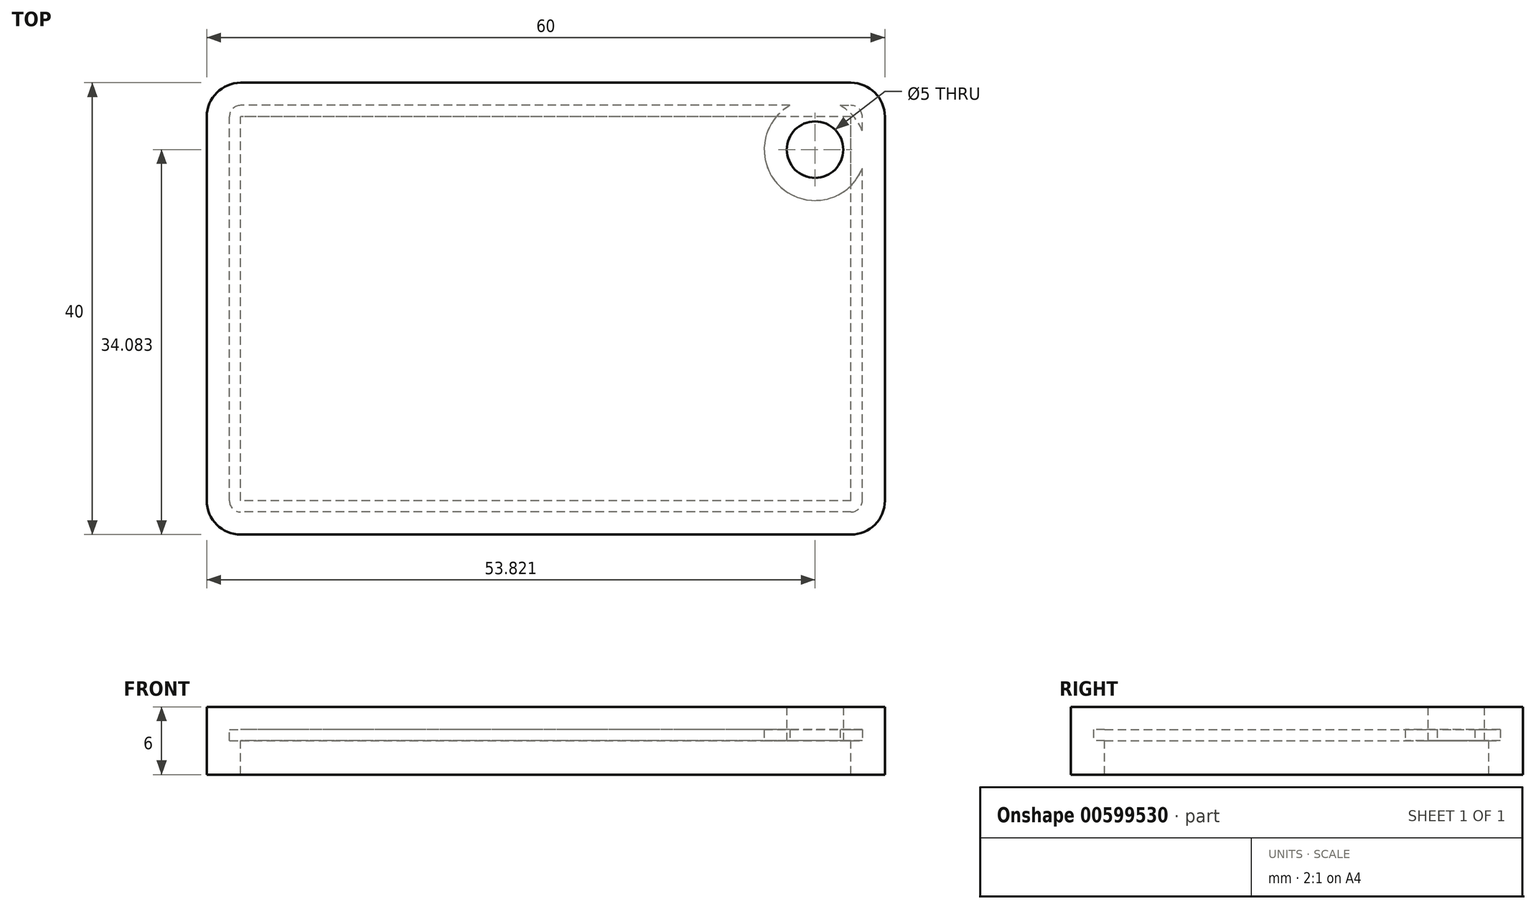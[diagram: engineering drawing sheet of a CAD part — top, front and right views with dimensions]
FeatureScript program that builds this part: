
annotation { "Feature Type Name" : "Feature", "Feature Type Description" : "" }
export const myFeature = defineFeature(function(context is Context, id is Id, definition is map)
    precondition{}
    {
        {
            var Q0;
            Q0=qCreatedBy(makeId("Top.planeOp"),FACE);
            var sketch = newSketch(context, id + "F0", { "sketchPlane" : qUnion([Q0])});
            skLineSegment(sketch, "E0.bottom", {"start": v(30, -20) * mm, "end": v(-30, -20) * mm});
            skLineSegment(sketch, "E0.top", {"start": v(30, 20) * mm, "end": v(-30, 20) * mm});
            skLineSegment(sketch, "E0.left", {"start": v(30, -20) * mm, "end": v(30, 20) * mm});
            skLineSegment(sketch, "E0.right", {"start": v(-30, -20) * mm, "end": v(-30, 20) * mm});
            skPoint(sketch, "E0.middle", {"position": v(0, 0) * mm});
            skSolve(sketch);
        }
        {
            var Q0;
            Q0=makeQuery(id+"F0.imprint","IMPRINT",FACE,{"disambiguationData":[TD([[makeQuery(id+"F0.imprint","IMPRINT",EDGE,{"derivedFrom":sQuery(id+"F0.wireOp",EDGE,"E0.bottom")}),-1.0]])]});
            extrude(context, id + "F1", {"entities" : qUnion([Q0]), "depth" : 6 * mm, "offsetDistance" : 25 * mm});
        }
        {
            var Q0;
            Q0=makeQuery(id+"F1.opExtrude","SWEPT_EDGE",EDGE,{"disambiguationData":[OSD([sQuery(id+"F0.wireOp",EDGE,"E0.bottom"),sQuery(id+"F0.wireOp",EDGE,"E0.right")])]});
            var Q1;
            Q1=makeQuery(id+"F1.opExtrude","SWEPT_EDGE",EDGE,{"disambiguationData":[OSD([sQuery(id+"F0.wireOp",EDGE,"E0.bottom"),sQuery(id+"F0.wireOp",EDGE,"E0.left")])]});
            var Q2;
            Q2=makeQuery(id+"F1.opExtrude","SWEPT_EDGE",EDGE,{"disambiguationData":[OSD([sQuery(id+"F0.wireOp",EDGE,"E0.top"),sQuery(id+"F0.wireOp",EDGE,"E0.right")])]});
            var Q3;
            Q3=makeQuery(id+"F1.opExtrude","SWEPT_EDGE",EDGE,{"disambiguationData":[OSD([sQuery(id+"F0.wireOp",EDGE,"E0.top"),sQuery(id+"F0.wireOp",EDGE,"E0.left")])]});
            fillet(context, id + "F2", {"entities" : qUnion([Q0, Q1, Q2, Q3]), "radius" : 3 * mm, "tangentPropagation" : true, "allowEdgeOverflow" : false});
        }
        {
            var Q0;
            Q0=makeQuery(id+"F1.opExtrude","CAP_FACE",FACE,{"disambiguationData":[OSD([sQuery(id+"F0.wireOp",EDGE,"E0.bottom"),sQuery(id+"F0.wireOp",EDGE,"E0.top"),sQuery(id+"F0.wireOp",EDGE,"E0.left"),sQuery(id+"F0.wireOp",EDGE,"E0.right")])],"isStart":true});
            shell(context, id + "F3", {"entities" : qUnion([Q0]), "thickness" : 3 * mm});
        }
        {
            var Q0;
            Q0=qCreatedBy(makeId("Top.planeOp"),FACE);
            var sketch = newSketch(context, id + "F4", { "sketchPlane" : qUnion([Q0])});
            skCircle(sketch, "E1", {"center": v(23.82, 14.08) * mm, "radius": 2.8 * mm});
            skPoint(sketch, "E1.first.point", {"position": v(25.9, 15.98) * mm});
            skPoint(sketch, "E1.second.point", {"position": v(22.28, 11.73) * mm});
            skPoint(sketch, "E1.third.point", {"position": v(21.43, 15.56) * mm});
            skSolve(sketch);
        }
        {
            var Q0;
            Q0=sQuery(id+"F4.wireOp",VERTEX,"E1.center");
            var Q1;
            Q1=makeQuery(id+"F1.opExtrude","SWEPT_BODY",BODY,{"disambiguationData":[OSD([sQuery(id+"F0.wireOp",EDGE,"E0.bottom"),sQuery(id+"F0.wireOp",EDGE,"E0.top"),sQuery(id+"F0.wireOp",EDGE,"E0.left"),sQuery(id+"F0.wireOp",EDGE,"E0.right")])]});
            hole(context, id + "F5", {"style" : HoleStyle.SIMPLE, "endStyle" : HoleEndStyle.THROUGH, "oppositeDirection" : true, "holeDiameter" : 5 * mm, "majorDiameter" : 5 * mm, "isTappedThrough" : true, "tappedDepth" : 12 * mm, "tapClearance" : 3, "locations" : qUnion([Q0]), "scope" : qUnion([Q1])});
        }
        {
            var Q0;
            Q0=makeQuery(id+"F3.opShell","OFFSET_FACE",FACE,{"disambiguationData":[OSD([sQuery(id+"F0.wireOp",EDGE,"E0.bottom"),sQuery(id+"F0.wireOp",EDGE,"E0.top"),sQuery(id+"F0.wireOp",EDGE,"E0.left"),sQuery(id+"F0.wireOp",EDGE,"E0.right")])]});
            shell(context, id + "F6", {"entities" : qUnion([Q0]), "thickness" : 2 * mm});
        }
    });
